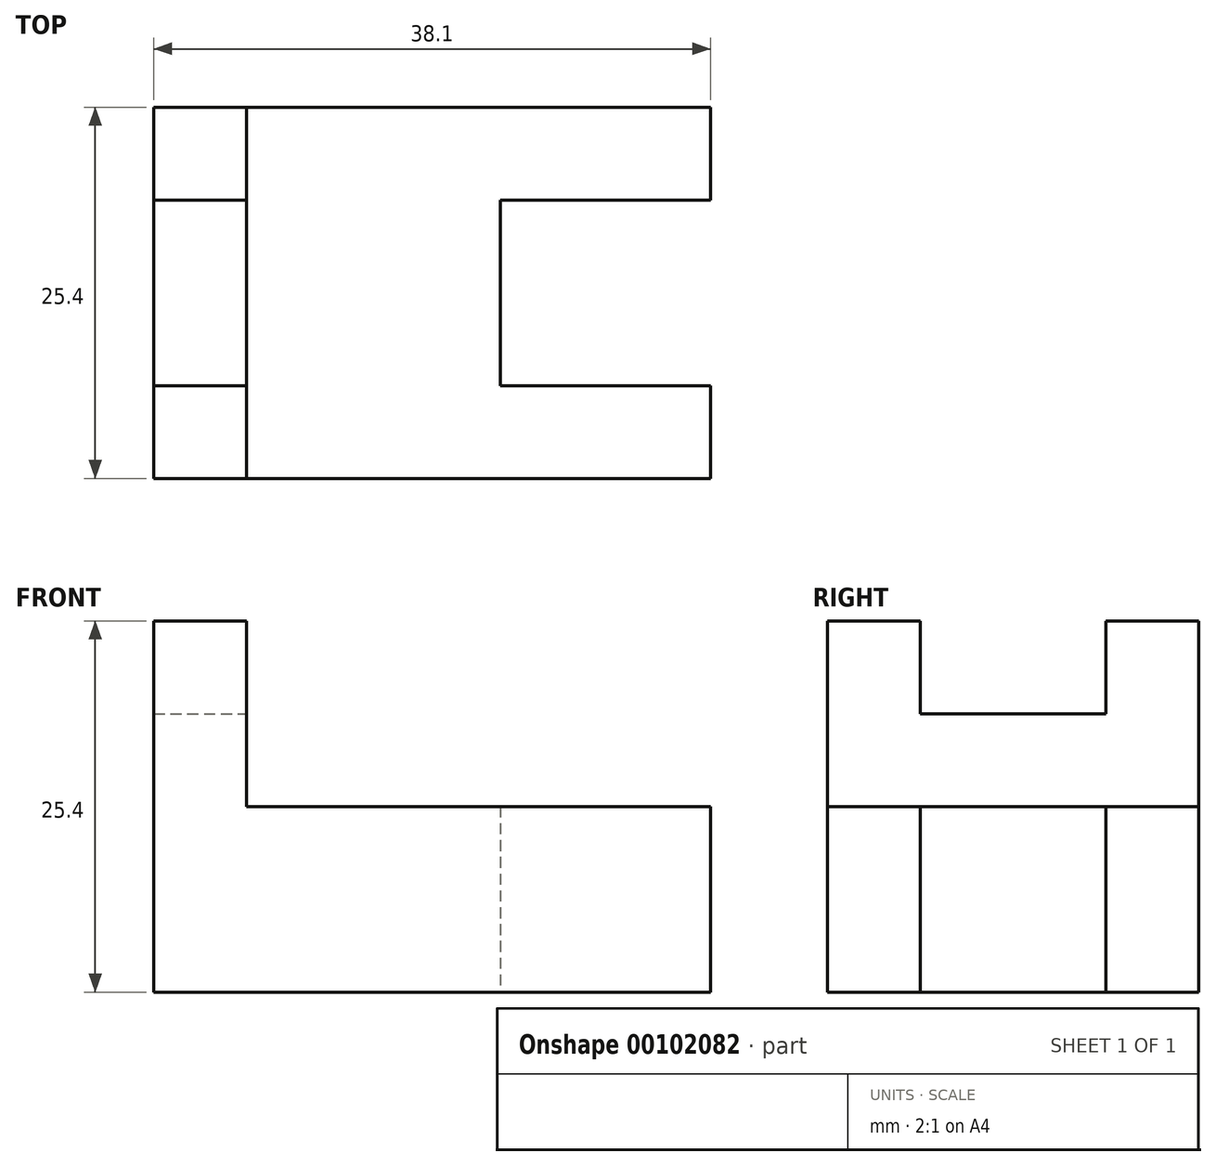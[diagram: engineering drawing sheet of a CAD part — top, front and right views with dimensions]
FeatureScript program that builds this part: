
annotation { "Feature Type Name" : "Feature", "Feature Type Description" : "" }
export const myFeature = defineFeature(function(context is Context, id is Id, definition is map)
    precondition{}
    {
        {
            var Q0;
            Q0=qCreatedBy(makeId("Top.planeOp"),FACE);
            var sketch = newSketch(context, id + "F0", { "sketchPlane" : qUnion([Q0])});
            skLineSegment(sketch, "E0", {"start": v(0, 0) * mm, "end": v(0, 25.4) * mm});
            skLineSegment(sketch, "E1", {"start": v(0, 25.4) * mm, "end": v(38.1, 25.4) * mm});
            skLineSegment(sketch, "E2", {"start": v(38.1, 25.4) * mm, "end": v(38.1, 19.05) * mm});
            skLineSegment(sketch, "E3", {"start": v(38.1, 19.05) * mm, "end": v(23.7, 19.05) * mm});
            skLineSegment(sketch, "E4", {"start": v(23.7, 19.05) * mm, "end": v(23.7, 6.35) * mm});
            skLineSegment(sketch, "E5", {"start": v(23.7, 6.35) * mm, "end": v(38.1, 6.35) * mm});
            skLineSegment(sketch, "E6", {"start": v(38.1, 6.35) * mm, "end": v(38.1, 0) * mm});
            skLineSegment(sketch, "E7", {"start": v(38.1, 0) * mm, "end": v(0, 0) * mm});
            skSolve(sketch);
        }
        {
            var Q0;
            Q0 = qSketchRegion(id + "F0", true);
            extrude(context, id + "F1", {"entities" : qUnion([Q0]), "depth" : 12.7 * mm});
        }
        {
            var Q0;
            Q0=makeQuery(id+"F1.opExtrude","CAP_FACE",FACE,{"disambiguationData":[OSD([sQuery(id+"F0.wireOp",EDGE,"E0"),sQuery(id+"F0.wireOp",EDGE,"E1"),sQuery(id+"F0.wireOp",EDGE,"E2"),sQuery(id+"F0.wireOp",EDGE,"E3"),sQuery(id+"F0.wireOp",EDGE,"E4"),sQuery(id+"F0.wireOp",EDGE,"E5"),sQuery(id+"F0.wireOp",EDGE,"E6"),sQuery(id+"F0.wireOp",EDGE,"E7")])],"isStart":false});
            var sketch = newSketch(context, id + "F2", { "sketchPlane" : qUnion([Q0])});
            skLineSegment(sketch, "E8.bottom", {"start": v(0, 25.4) * mm, "end": v(6.35, 25.4) * mm});
            skLineSegment(sketch, "E8.top", {"start": v(0, 0) * mm, "end": v(6.35, 0) * mm});
            skLineSegment(sketch, "E8.left", {"start": v(0, 25.4) * mm, "end": v(0, 0) * mm});
            skLineSegment(sketch, "E8.right", {"start": v(6.35, 25.4) * mm, "end": v(6.35, 0) * mm});
            skSolve(sketch);
        }
        {
            var Q0;
            Q0 = qSketchRegion(id + "F2", true);
            extrude(context, id + "F3", {"entities" : qUnion([Q0]), "operationType" : NewBodyOperationType.ADD, "depth" : 12.7 * mm});
        }
        {
            var Q0;
            Q0=makeQuery(id+"F3.opExtrude","SWEPT_FACE",FACE,{"disambiguationData":[OSD([sQuery(id+"F2.wireOp",EDGE,"E8.right")])]});
            var sketch = newSketch(context, id + "F4", { "sketchPlane" : qUnion([Q0])});
            skLineSegment(sketch, "E9.bottom", {"start": v(6.35, 25.4) * mm, "end": v(19.05, 25.4) * mm});
            skLineSegment(sketch, "E9.top", {"start": v(6.35, 19.05) * mm, "end": v(19.05, 19.05) * mm});
            skLineSegment(sketch, "E9.left", {"start": v(6.35, 25.4) * mm, "end": v(6.35, 19.05) * mm});
            skLineSegment(sketch, "E9.right", {"start": v(19.05, 25.4) * mm, "end": v(19.05, 19.05) * mm});
            skSolve(sketch);
        }
        {
            var Q0;
            Q0 = qSketchRegion(id + "F4", true);
            extrude(context, id + "F5", {"entities" : qUnion([Q0]), "operationType" : NewBodyOperationType.REMOVE, "oppositeDirection" : true, "depth" : 25.4 * mm});
        }
    });
